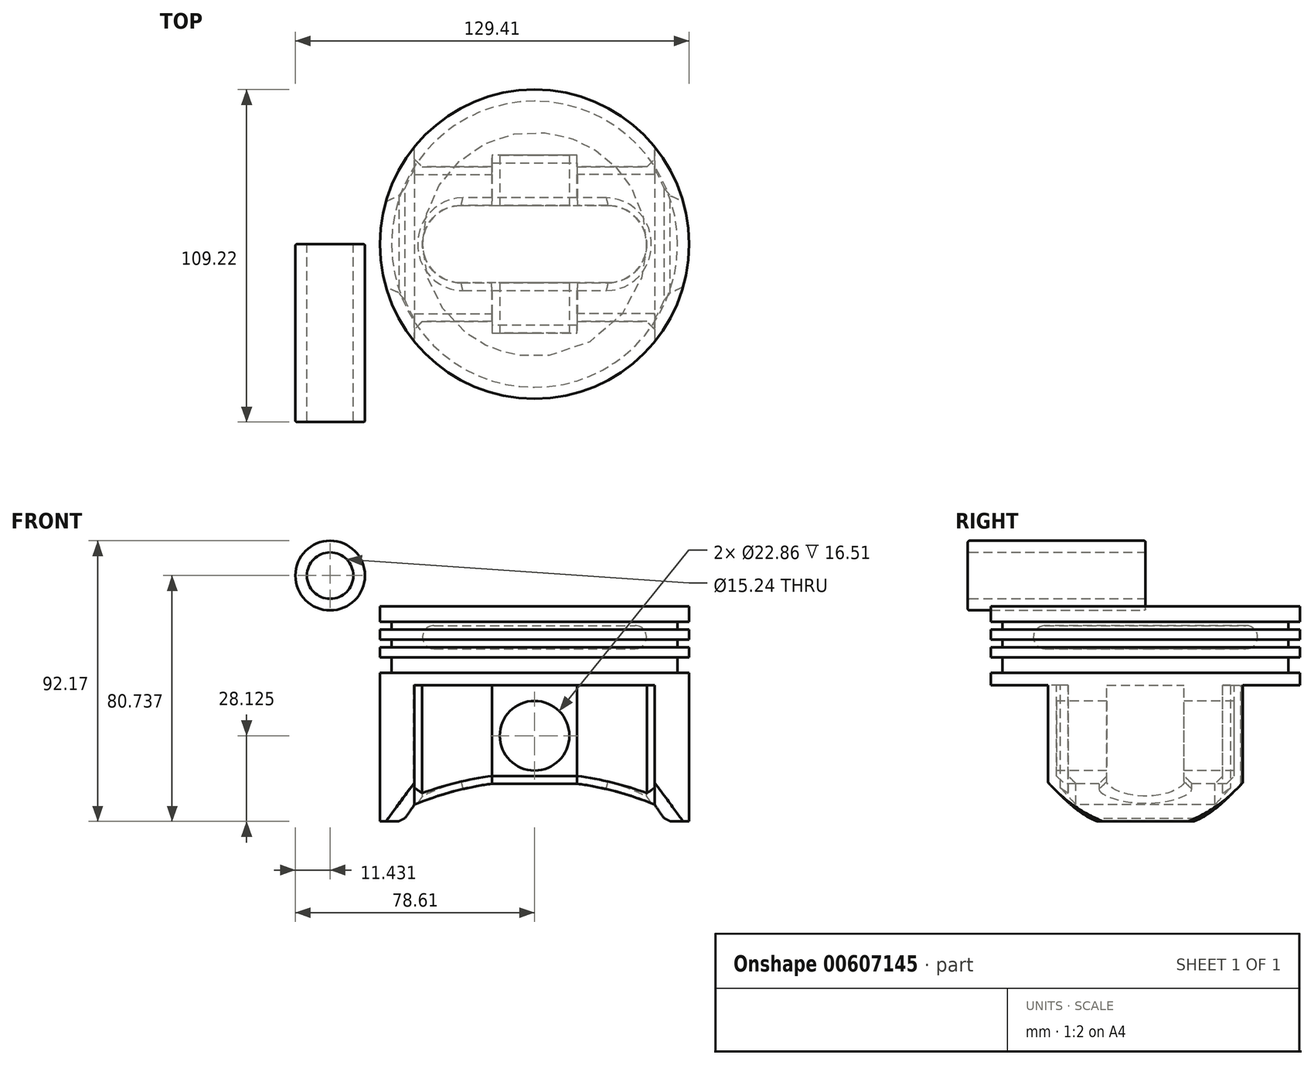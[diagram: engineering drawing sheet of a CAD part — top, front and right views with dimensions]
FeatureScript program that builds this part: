
annotation { "Feature Type Name" : "Feature", "Feature Type Description" : "" }
export const myFeature = defineFeature(function(context is Context, id is Id, definition is map)
    precondition{}
    {
        {
            var Q0;
            Q0=qCreatedBy(makeId("Front.planeOp"),FACE);
            var sketch = newSketch(context, id + "F0", { "sketchPlane" : qUnion([Q0])});
            skLineSegment(sketch, "E0", {"start": v(0, 42.54) * mm, "end": v(-50.8, 42.54) * mm});
            skLineSegment(sketch, "E1", {"start": v(-50.8, 42.54) * mm, "end": v(-50.8, 37.46) * mm});
            skLineSegment(sketch, "E2", {"start": v(-50.8, 37.46) * mm, "end": v(-47, 37.46) * mm});
            skLineSegment(sketch, "E3", {"start": v(-47, 37.46) * mm, "end": v(-47, 34.92) * mm});
            skLineSegment(sketch, "E4", {"start": v(-47, 34.92) * mm, "end": v(-50.8, 34.92) * mm});
            skLineSegment(sketch, "E5", {"start": v(-50.8, 34.92) * mm, "end": v(-50.8, 31.62) * mm});
            skLineSegment(sketch, "E6", {"start": v(-50.8, 31.62) * mm, "end": v(-47, 31.62) * mm});
            skLineSegment(sketch, "E7", {"start": v(-47, 31.62) * mm, "end": v(-47, 29.08) * mm});
            skLineSegment(sketch, "E8", {"start": v(-47, 29.08) * mm, "end": v(-50.8, 29.08) * mm});
            skLineSegment(sketch, "E9", {"start": v(-50.8, 29.08) * mm, "end": v(-50.8, 25.78) * mm});
            skLineSegment(sketch, "E10", {"start": v(-50.8, 25.78) * mm, "end": v(-47, 25.78) * mm});
            skLineSegment(sketch, "E11", {"start": v(-47, 25.78) * mm, "end": v(-47, 20.7) * mm});
            skLineSegment(sketch, "E12", {"start": v(-47, 20.7) * mm, "end": v(-50.8, 20.7) * mm});
            skLineSegment(sketch, "E13", {"start": v(-50.8, 20.7) * mm, "end": v(-50.8, 16.53) * mm});
            skLineSegment(sketch, "E14", {"start": v(-47, 24.5) * mm, "end": v(-50.23, 24.5) * mm, "construction": true});
            skLineSegment(sketch, "E15", {"start": v(-47, 21.97) * mm, "end": v(-49.28, 21.97) * mm, "construction": true});
            skLineSegment(sketch, "E16", {"start": v(-50.8, 16.53) * mm, "end": v(0, 16.53) * mm});
            skLineSegment(sketch, "E17", {"start": v(0, 16.53) * mm, "end": v(0, 42.54) * mm});
            skLineSegment(sketch, "E18", {"start": v(0, 36.19) * mm, "end": v(-33.02, 36.19) * mm});
            skLineSegment(sketch, "E19", {"start": v(-33.02, 28.57) * mm, "end": v(0, 28.57) * mm});
            skArc(sketch, "E20", {"start": v(-33.02, 36.19) * mm, "mid": v(-36.83, 32.38) * mm, "end": v(-33.02, 28.57) * mm});
            skSolve(sketch);
        }
        {
            var Q0;
            {var subQ0=sQuery(id+"F0.wireOp",EDGE,"E0");Q0=makeQuery(id+"F0.imprint","IMPRINT",FACE,{"disambiguationData":[TD([[makeQuery(id+"F0.imprint","IMPRINT",EDGE,{"derivedFrom":subQ0}),1.0]])]});}
            var Q1;
            Q1=sQuery(id+"F0.wireOp",EDGE,"E17");
            revolve(context, id + "F1", {"entities" : qUnion([Q0]), "axis" : qUnion([Q1]), "revolveType" : RevolveType.FULL});
        }
        {
            var Q0;
            Q0=makeQuery(id+"F1.opRevolve","SWEPT_FACE",FACE,{"disambiguationData":[OSD([sQuery(id+"F0.wireOp",EDGE,"E16")])]});
            var sketch = newSketch(context, id + "F2", { "sketchPlane" : qUnion([Q0])});
            skLineSegment(sketch, "E21", {"start": v(0, 12.7) * mm, "end": v(-24.13, 12.7) * mm});
            skLineSegment(sketch, "E22", {"start": v(-13.97, 25.4) * mm, "end": v(-39.45, 25.4) * mm});
            skLineSegment(sketch, "E23", {"start": v(-39.45, 25.4) * mm, "end": v(-39.45, 32) * mm});
            skLineSegment(sketch, "E24.MirrorCS", {"start": v(0, -12.7) * mm, "end": v(-24.13, -12.7) * mm});
            skLineSegment(sketch, "E25.MirrorCS", {"start": v(-13.97, -25.4) * mm, "end": v(-39.45, -25.4) * mm});
            skLineSegment(sketch, "E26.MirrorCS", {"start": v(-39.45, -25.4) * mm, "end": v(-39.45, -32) * mm});
            skArc(sketch, "E27", {"start": v(-24.13, 12.7) * mm, "mid": v(-36.83, 0) * mm, "end": v(-24.13, -12.7) * mm});
            skLineSegment(sketch, "E28.MirrorCS", {"start": v(13.97, 25.4) * mm, "end": v(39.45, 25.4) * mm});
            skLineSegment(sketch, "E29.MirrorCS", {"start": v(0, 12.7) * mm, "end": v(24.13, 12.7) * mm});
            skArc(sketch, "E30.MirrorCS", {"start": v(24.13, 12.7) * mm, "mid": v(36.83, 0) * mm, "end": v(24.13, -12.7) * mm});
            skLineSegment(sketch, "E31.MirrorCS", {"start": v(39.45, -25.4) * mm, "end": v(39.45, -32) * mm});
            skLineSegment(sketch, "E32.MirrorCS", {"start": v(13.97, -25.4) * mm, "end": v(39.45, -25.4) * mm});
            skLineSegment(sketch, "E33.MirrorCS", {"start": v(0, -12.7) * mm, "end": v(24.13, -12.7) * mm});
            skLineSegment(sketch, "E34.MirrorCS", {"start": v(39.45, 25.4) * mm, "end": v(39.45, 32) * mm});
            skLineSegment(sketch, "E35", {"start": v(-13.97, 25.4) * mm, "end": v(-13.97, 29.21) * mm});
            skLineSegment(sketch, "E36", {"start": v(-13.97, 29.21) * mm, "end": v(0, 29.21) * mm});
            skLineSegment(sketch, "E37.MirrorCS", {"start": v(13.97, 29.21) * mm, "end": v(0, 29.21) * mm});
            skLineSegment(sketch, "E38.MirrorCS", {"start": v(13.97, 25.4) * mm, "end": v(13.97, 29.21) * mm});
            skLineSegment(sketch, "E39.MirrorCS", {"start": v(-13.97, -29.21) * mm, "end": v(0, -29.21) * mm});
            skLineSegment(sketch, "E40.MirrorCS", {"start": v(-13.97, -25.4) * mm, "end": v(-13.97, -29.21) * mm});
            skLineSegment(sketch, "E41.MirrorCS", {"start": v(13.97, -29.21) * mm, "end": v(0, -29.21) * mm});
            skLineSegment(sketch, "E42.MirrorCS", {"start": v(13.97, -25.4) * mm, "end": v(13.97, -29.21) * mm});
            skPoint(sketch, "E43.orphan", {"position": v(0, 25.4) * mm});
            skPoint(sketch, "E44.orphan", {"position": v(0, -25.4) * mm});
            skSolve(sketch);
        }
        {
            var Q0;
            Q0=makeQuery(id+"F2.imprint","IMPRINT",FACE,{"disambiguationData":[TD([[makeQuery(id+"F2.imprint","IMPRINT",EDGE,{"derivedFrom":sQuery(id+"F2.wireOp",EDGE,"E21")}),-1.0]])]});
            extrude(context, id + "F3", {"entities" : qUnion([Q0]), "operationType" : NewBodyOperationType.ADD, "depth" : 50.8 * mm, "offsetDistance" : 25.4 * mm});
        }
        {
            var Q0;
            Q0=makeQuery(id+"F3.opExtrude","SWEPT_FACE",FACE,{"disambiguationData":[OSD([sQuery(id+"F2.wireOp",EDGE,"E36"),sQuery(id+"F2.wireOp",EDGE,"E37.MirrorCS")])]});
            var sketch = newSketch(context, id + "F4", { "sketchPlane" : qUnion([Q0])});
            skCircle(sketch, "E45", {"center": v(0, 0) * mm, "radius": 11.43 * mm});
            skLineSegment(sketch, "E46", {"start": v(-50.8, -34.27) * mm, "end": v(-50.8, 20.7) * mm});
            skLineSegment(sketch, "E47", {"start": v(50.8, 20.7) * mm, "end": v(50.8, -34.27) * mm});
            skPoint(sketch, "E48.0.end.orphan", {"position": v(-50.8, -34.27) * mm});
            skPoint(sketch, "E48.0.start.orphan", {"position": v(-39.45, -34.27) * mm});
            skPoint(sketch, "E49.0.end.orphan", {"position": v(50.8, -34.27) * mm});
            skPoint(sketch, "E49.0.start.orphan", {"position": v(39.45, -34.27) * mm});
            skPoint(sketch, "E50", {"position": v(-50.8, -28.13) * mm});
            skPoint(sketch, "E51", {"position": v(50.8, -28.13) * mm});
            skArc(sketch, "E52", {"start": v(39.45, -22.62) * mm, "mid": v(26.93, -18.38) * mm, "end": v(13.97, -15.76) * mm});
            skLineSegment(sketch, "E53", {"start": v(-13.97, -15.76) * mm, "end": v(13.97, -15.76) * mm});
            skArc(sketch, "E54.trimOffspring", {"start": v(-13.97, -15.76) * mm, "mid": v(-26.93, -18.38) * mm, "end": v(-39.45, -22.62) * mm});
            skLineSegment(sketch, "E55", {"start": v(-50.8, -28.13) * mm, "end": v(-43.3, -28.13) * mm});
            skLineSegment(sketch, "E56.MirrorCS", {"start": v(50.8, -28.13) * mm, "end": v(43.3, -28.13) * mm});
            skLineSegment(sketch, "E57", {"start": v(-50.8, -28.13) * mm, "end": v(-60.85, -30.62) * mm});
            skLineSegment(sketch, "E58", {"start": v(-60.85, -30.62) * mm, "end": v(-59.3, -53.17) * mm});
            skLineSegment(sketch, "E59", {"start": v(-59.3, -53.17) * mm, "end": v(61.9, -50.2) * mm});
            skLineSegment(sketch, "E60", {"start": v(61.9, -50.2) * mm, "end": v(64.49, -26.6) * mm});
            skLineSegment(sketch, "E61", {"start": v(64.49, -26.6) * mm, "end": v(50.8, -28.13) * mm});
            skLineSegment(sketch, "E62", {"start": v(43.3, -28.13) * mm, "end": v(39.45, -22.62) * mm});
            skPoint(sketch, "E63.MirrorCS.start.orphan", {"position": v(39.45, -28.13) * mm});
            skLineSegment(sketch, "E64.MirrorCS", {"start": v(-43.3, -28.13) * mm, "end": v(-39.45, -22.62) * mm});
            skPoint(sketch, "E65.start.orphan", {"position": v(-39.45, -28.13) * mm});
            skSolve(sketch);
        }
        {
            var Q0;
            {var subQ0=sQuery(id+"F4.wireOp",EDGE,"E52");Q0=makeQuery(id+"F4.imprint","IMPRINT",FACE,{"disambiguationData":[TD([[makeQuery(id+"F4.imprint","IMPRINT",EDGE,{"derivedFrom":subQ0}),1.0]])]});}
            var Q1;
            Q1=makeQuery(id+"F4.imprint","IMPRINT",FACE,{"disambiguationData":[TD([[makeQuery(id+"F4.imprint","IMPRINT",EDGE,{"derivedFrom":sQuery(id+"F4.wireOp",EDGE,"E45")}),1.0]])]});
            var Q2;
            {var subQ0=sQuery(id+"F4.wireOp",EDGE,"E53");Q2=makeQuery(id+"F4.imprint","IMPRINT",FACE,{"disambiguationData":[TD([[makeQuery(id+"F4.imprint","IMPRINT",EDGE,{"derivedFrom":subQ0}),-1.0]])]});}
            extrude(context, id + "F5", {"entities" : qUnion([Q0, Q1, Q2]), "operationType" : NewBodyOperationType.REMOVE, "oppositeDirection" : true, "depth" : 160.53 * mm, "offsetDistance" : 25.4 * mm, "symmetric" : true});
        }
        {
            var Q0;
            Q0=makeQuery(id+"F5.boolean.opBoolean","INTERSECT",EDGE,{"derivedFrom":[makeQuery(id+"F3.opExtrude","SWEPT_FACE",FACE,{"disambiguationData":[OSD([sQuery(id+"F2.wireOp",EDGE,"E30.MirrorCS")])]}),makeQuery(id+"F5.opExtrude","SWEPT_FACE",FACE,{"disambiguationData":[OSD([sQuery(id+"F4.wireOp",EDGE,"E52")])]})]});
            var Q1;
            Q1=makeQuery(id+"F5.boolean.opBoolean","INTERSECT",EDGE,{"derivedFrom":[makeQuery(id+"F3.opExtrude","SWEPT_FACE",FACE,{"disambiguationData":[OSD([sQuery(id+"F2.wireOp",EDGE,"E24.MirrorCS"),sQuery(id+"F2.wireOp",EDGE,"E33.MirrorCS")])]}),makeQuery(id+"F5.opExtrude","SWEPT_FACE",FACE,{"disambiguationData":[OSD([sQuery(id+"F4.wireOp",EDGE,"E53")])]})]});
            var Q2;
            Q2=makeQuery(id+"F5.boolean.opBoolean","INTERSECT",EDGE,{"derivedFrom":[makeQuery(id+"F3.opExtrude","SWEPT_FACE",FACE,{"disambiguationData":[OSD([sQuery(id+"F2.wireOp",EDGE,"E24.MirrorCS"),sQuery(id+"F2.wireOp",EDGE,"E33.MirrorCS")])]}),makeQuery(id+"F5.opExtrude","SWEPT_FACE",FACE,{"disambiguationData":[OSD([sQuery(id+"F4.wireOp",EDGE,"E54.trimOffspring")])]})]});
            var Q3;
            Q3=makeQuery(id+"F5.boolean.opBoolean","INTERSECT",EDGE,{"derivedFrom":[makeQuery(id+"F3.opExtrude","SWEPT_FACE",FACE,{"disambiguationData":[OSD([sQuery(id+"F2.wireOp",EDGE,"E21"),sQuery(id+"F2.wireOp",EDGE,"E29.MirrorCS")])]}),makeQuery(id+"F5.opExtrude","SWEPT_FACE",FACE,{"disambiguationData":[OSD([sQuery(id+"F4.wireOp",EDGE,"E53")])]})]});
            var Q4;
            Q4=makeQuery(id+"F5.boolean.opBoolean","INTERSECT",EDGE,{"derivedFrom":[makeQuery(id+"F3.opExtrude","SWEPT_FACE",FACE,{"disambiguationData":[OSD([sQuery(id+"F2.wireOp",EDGE,"E32.MirrorCS")])]}),makeQuery(id+"F5.opExtrude","SWEPT_FACE",FACE,{"disambiguationData":[OSD([sQuery(id+"F4.wireOp",EDGE,"E52")])]})]});
            var Q5;
            Q5=makeQuery(id+"F5.boolean.opBoolean","INTERSECT",EDGE,{"derivedFrom":[makeQuery(id+"F3.opExtrude","SWEPT_FACE",FACE,{"disambiguationData":[OSD([sQuery(id+"F2.wireOp",EDGE,"E25.MirrorCS")])]}),makeQuery(id+"F5.opExtrude","SWEPT_FACE",FACE,{"disambiguationData":[OSD([sQuery(id+"F4.wireOp",EDGE,"E54.trimOffspring")])]})]});
            var Q6;
            Q6=makeQuery(id+"F3.opExtrude","CAP_EDGE",EDGE,{"disambiguationData":[OSD([sQuery(id+"F2.wireOp",EDGE,"E25.MirrorCS")])],"isStart":true});
            var Q7;
            Q7=makeQuery(id+"F3.opExtrude","CAP_EDGE",EDGE,{"disambiguationData":[OSD([sQuery(id+"F2.wireOp",EDGE,"E32.MirrorCS")])],"isStart":true});
            var Q8;
            Q8=makeQuery(id+"F5.boolean.opBoolean","INTERSECT",EDGE,{"derivedFrom":[makeQuery(id+"F3.opExtrude","SWEPT_FACE",FACE,{"disambiguationData":[OSD([sQuery(id+"F2.wireOp",EDGE,"E22")])]}),makeQuery(id+"F5.opExtrude","SWEPT_FACE",FACE,{"disambiguationData":[OSD([sQuery(id+"F4.wireOp",EDGE,"E54.trimOffspring")])]})]});
            var Q9;
            Q9=makeQuery(id+"F5.boolean.opBoolean","INTERSECT",EDGE,{"derivedFrom":[makeQuery(id+"F3.opExtrude","SWEPT_FACE",FACE,{"disambiguationData":[OSD([sQuery(id+"F2.wireOp",EDGE,"E28.MirrorCS")])]}),makeQuery(id+"F5.opExtrude","SWEPT_FACE",FACE,{"disambiguationData":[OSD([sQuery(id+"F4.wireOp",EDGE,"E52")])]})]});
            var Q10;
            Q10=makeQuery(id+"F3.opExtrude","CAP_EDGE",EDGE,{"disambiguationData":[OSD([sQuery(id+"F2.wireOp",EDGE,"E28.MirrorCS")])],"isStart":true});
            var Q11;
            Q11=makeQuery(id+"F3.opExtrude","CAP_EDGE",EDGE,{"disambiguationData":[OSD([sQuery(id+"F2.wireOp",EDGE,"E22")])],"isStart":true});
            var Q12;
            Q12=makeQuery(id+"F3.opExtrude","CAP_EDGE",EDGE,{"disambiguationData":[OSD([sQuery(id+"F2.wireOp",EDGE,"E36"),sQuery(id+"F2.wireOp",EDGE,"E37.MirrorCS")])],"isStart":true});
            var Q13;
            Q13=makeQuery(id+"F3.opExtrude","CAP_EDGE",EDGE,{"disambiguationData":[OSD([sQuery(id+"F2.wireOp",EDGE,"E35")])],"isStart":true});
            var Q14;
            Q14=makeQuery(id+"F3.opExtrude","CAP_EDGE",EDGE,{"disambiguationData":[OSD([sQuery(id+"F2.wireOp",EDGE,"E38.MirrorCS")])],"isStart":true});
            var Q15;
            Q15=makeQuery(id+"F3.opExtrude","CAP_EDGE",EDGE,{"disambiguationData":[OSD([sQuery(id+"F2.wireOp",EDGE,"E39.MirrorCS"),sQuery(id+"F2.wireOp",EDGE,"E41.MirrorCS")])],"isStart":true});
            var Q16;
            Q16=makeQuery(id+"F3.opExtrude","CAP_EDGE",EDGE,{"disambiguationData":[OSD([sQuery(id+"F2.wireOp",EDGE,"E40.MirrorCS")])],"isStart":true});
            var Q17;
            Q17=makeQuery(id+"F3.opExtrude","CAP_EDGE",EDGE,{"disambiguationData":[OSD([sQuery(id+"F2.wireOp",EDGE,"E42.MirrorCS")])],"isStart":true});
            chamfer(context, id + "F6", {"entities" : qUnion([Q0, Q1, Q2, Q3, Q4, Q5, Q6, Q7, Q8, Q9, Q10, Q11, Q12, Q13, Q14, Q15, Q16, Q17]), "width" : 2.54 * mm, "tangentPropagation" : true});
        }
        {
            var Q0;
            Q0=makeQuery(id+"F3.opExtrude","SWEPT_EDGE",EDGE,{"disambiguationData":[OSD([sQuery(id+"F2.wireOp",EDGE,"E25.MirrorCS"),sQuery(id+"F2.wireOp",EDGE,"E26.MirrorCS")])]});
            var Q1;
            Q1=makeQuery(id+"F3.opExtrude","SWEPT_EDGE",EDGE,{"disambiguationData":[OSD([sQuery(id+"F2.wireOp",EDGE,"E31.MirrorCS"),sQuery(id+"F2.wireOp",EDGE,"E32.MirrorCS")])]});
            var Q2;
            Q2=makeQuery(id+"F5.boolean.opBoolean","INTERSECT",EDGE,{"derivedFrom":[makeQuery(id+"F3.opExtrude","SWEPT_FACE",FACE,{"disambiguationData":[OSD([sQuery(id+"F2.wireOp",EDGE,"E39.MirrorCS"),sQuery(id+"F2.wireOp",EDGE,"E41.MirrorCS")])]}),makeQuery(id+"F5.opExtrude","SWEPT_FACE",FACE,{"disambiguationData":[OSD([sQuery(id+"F4.wireOp",EDGE,"E53")])]})]});
            var Q3;
            {var subQ0=sQuery(id+"F4.wireOp",EDGE,"E53");Q3=makeQuery(id+"F5.boolean.opBoolean","COPY",EDGE,{"disambiguationData":[topologyDisambiguationEdgeConnected([makeQuery(id+"F3.opExtrude","SWEPT_FACE",FACE,{"disambiguationData":[OSD([sQuery(id+"F2.wireOp",EDGE,"E40.MirrorCS")])]}),makeQuery(id+"F5.opExtrude","SWEPT_FACE",FACE,{"disambiguationData":[OSD([subQ0])]})])],"derivedFrom":makeQuery(id+"F5.opExtrude","SWEPT_EDGE",EDGE,{"disambiguationData":[OSD([sQuery(id+"F2.wireOp",EDGE,"E35"),sQuery(id+"F2.wireOp",EDGE,"E36"),subQ0,sQuery(id+"F4.wireOp",EDGE,"E54.trimOffspring")])]})});}
            var Q4;
            {var subQ0=sQuery(id+"F4.wireOp",EDGE,"E53");Q4=makeQuery(id+"F5.boolean.opBoolean","COPY",EDGE,{"disambiguationData":[topologyDisambiguationEdgeConnected([makeQuery(id+"F3.opExtrude","SWEPT_FACE",FACE,{"disambiguationData":[OSD([sQuery(id+"F2.wireOp",EDGE,"E42.MirrorCS")])]}),makeQuery(id+"F5.opExtrude","SWEPT_FACE",FACE,{"disambiguationData":[OSD([subQ0])]})])],"derivedFrom":makeQuery(id+"F5.opExtrude","SWEPT_EDGE",EDGE,{"disambiguationData":[OSD([sQuery(id+"F2.wireOp",EDGE,"E37.MirrorCS"),sQuery(id+"F2.wireOp",EDGE,"E38.MirrorCS"),sQuery(id+"F4.wireOp",EDGE,"E52"),subQ0])]})});}
            var Q5;
            Q5=makeQuery(id+"F3.opExtrude","SWEPT_EDGE",EDGE,{"disambiguationData":[OSD([sQuery(id+"F2.wireOp",EDGE,"E28.MirrorCS"),sQuery(id+"F2.wireOp",EDGE,"E34.MirrorCS")])]});
            var Q6;
            Q6=makeQuery(id+"F3.opExtrude","SWEPT_EDGE",EDGE,{"disambiguationData":[OSD([sQuery(id+"F2.wireOp",EDGE,"E22"),sQuery(id+"F2.wireOp",EDGE,"E23")])]});
            var Q7;
            Q7=makeQuery(id+"F5.boolean.opBoolean","INTERSECT",EDGE,{"derivedFrom":[makeQuery(id+"F3.opExtrude","SWEPT_FACE",FACE,{"disambiguationData":[OSD([sQuery(id+"F2.wireOp",EDGE,"E36"),sQuery(id+"F2.wireOp",EDGE,"E37.MirrorCS")])]}),makeQuery(id+"F5.opExtrude","SWEPT_FACE",FACE,{"disambiguationData":[OSD([sQuery(id+"F4.wireOp",EDGE,"E53")])]})]});
            var Q8;
            {var subQ0=sQuery(id+"F2.wireOp",EDGE,"E38.MirrorCS");var subQ1=sQuery(id+"F4.wireOp",EDGE,"E53");Q8=makeQuery(id+"F5.boolean.opBoolean","COPY",EDGE,{"disambiguationData":[topologyDisambiguationEdgeConnected([makeQuery(id+"F3.opExtrude","SWEPT_FACE",FACE,{"disambiguationData":[OSD([subQ0])]}),makeQuery(id+"F5.opExtrude","SWEPT_FACE",FACE,{"disambiguationData":[OSD([subQ1])]})])],"derivedFrom":makeQuery(id+"F5.opExtrude","SWEPT_EDGE",EDGE,{"disambiguationData":[OSD([sQuery(id+"F2.wireOp",EDGE,"E37.MirrorCS"),subQ0,sQuery(id+"F4.wireOp",EDGE,"E52"),subQ1])]})});}
            var Q9;
            {var subQ0=sQuery(id+"F2.wireOp",EDGE,"E35");var subQ1=sQuery(id+"F4.wireOp",EDGE,"E53");Q9=makeQuery(id+"F5.boolean.opBoolean","COPY",EDGE,{"disambiguationData":[topologyDisambiguationEdgeConnected([makeQuery(id+"F3.opExtrude","SWEPT_FACE",FACE,{"disambiguationData":[OSD([subQ0])]}),makeQuery(id+"F5.opExtrude","SWEPT_FACE",FACE,{"disambiguationData":[OSD([subQ1])]})])],"derivedFrom":makeQuery(id+"F5.opExtrude","SWEPT_EDGE",EDGE,{"disambiguationData":[OSD([subQ0,sQuery(id+"F2.wireOp",EDGE,"E36"),subQ1,sQuery(id+"F4.wireOp",EDGE,"E54.trimOffspring")])]})});}
            var Q10;
            {var subQ0=sQuery(id+"F0.wireOp",EDGE,"E16");var subQ1=sQuery(id+"F0.wireOp",EDGE,"E13");var subQ2=makeQuery(id+"F1.opRevolve","SWEPT_EDGE",EDGE,{"disambiguationData":[OSD([subQ1,subQ0])]});Q10=makeQuery(id+"F5.boolean.opBoolean","INTERSECT",EDGE,{"disambiguationData":[OD(0.0)],"derivedFrom":[makeQuery(id+"F3.boolean.opBoolean","MERGE",FACE,{"derivedFrom":[makeQuery(id+"F1.opRevolve","SWEPT_FACE",FACE,{"disambiguationData":[OSD([subQ1])]}),makeQuery(id+"F3.opExtrude","SWEPT_FACE",FACE,{"disambiguationData":[OSD([subQ1,subQ0]),TDD([makeQuery(id+"F2.imprint","IMPRINT",EDGE,{"disambiguationData":[TD([[makeQuery(id+"F2.imprint","INTERSECT",VERTEX,{"derivedFrom":[subQ2,sQuery(id+"F2.wireOp",EDGE,"E23")]}),-1.0]])],"derivedFrom":subQ2})])]}),makeQuery(id+"F3.opExtrude","SWEPT_FACE",FACE,{"disambiguationData":[OSD([subQ1,subQ0]),TDD([makeQuery(id+"F2.imprint","IMPRINT",EDGE,{"disambiguationData":[TD([[makeQuery(id+"F2.imprint","INTERSECT",VERTEX,{"derivedFrom":[subQ2,sQuery(id+"F2.wireOp",EDGE,"E31.MirrorCS")]}),-1.0]])],"derivedFrom":subQ2})])]})]}),makeQuery(id+"F5.opExtrude","SWEPT_FACE",FACE,{"disambiguationData":[OSD([sQuery(id+"F4.wireOp",EDGE,"E62")])]})]});}
            var Q11;
            {var subQ0=sQuery(id+"F0.wireOp",EDGE,"E16");var subQ1=sQuery(id+"F0.wireOp",EDGE,"E13");var subQ2=makeQuery(id+"F1.opRevolve","SWEPT_EDGE",EDGE,{"disambiguationData":[OSD([subQ1,subQ0])]});Q11=makeQuery(id+"F5.boolean.opBoolean","INTERSECT",EDGE,{"disambiguationData":[OD(1.0)],"derivedFrom":[makeQuery(id+"F3.boolean.opBoolean","MERGE",FACE,{"derivedFrom":[makeQuery(id+"F1.opRevolve","SWEPT_FACE",FACE,{"disambiguationData":[OSD([subQ1])]}),makeQuery(id+"F3.opExtrude","SWEPT_FACE",FACE,{"disambiguationData":[OSD([subQ1,subQ0]),TDD([makeQuery(id+"F2.imprint","IMPRINT",EDGE,{"disambiguationData":[TD([[makeQuery(id+"F2.imprint","INTERSECT",VERTEX,{"derivedFrom":[subQ2,sQuery(id+"F2.wireOp",EDGE,"E23")]}),-1.0]])],"derivedFrom":subQ2})])]}),makeQuery(id+"F3.opExtrude","SWEPT_FACE",FACE,{"disambiguationData":[OSD([subQ1,subQ0]),TDD([makeQuery(id+"F2.imprint","IMPRINT",EDGE,{"disambiguationData":[TD([[makeQuery(id+"F2.imprint","INTERSECT",VERTEX,{"derivedFrom":[subQ2,sQuery(id+"F2.wireOp",EDGE,"E31.MirrorCS")]}),-1.0]])],"derivedFrom":subQ2})])]})]}),makeQuery(id+"F5.opExtrude","SWEPT_FACE",FACE,{"disambiguationData":[OSD([sQuery(id+"F4.wireOp",EDGE,"E64.MirrorCS")])]})]});}
            var Q12;
            {var subQ0=sQuery(id+"F0.wireOp",EDGE,"E16");var subQ1=sQuery(id+"F0.wireOp",EDGE,"E13");var subQ2=makeQuery(id+"F1.opRevolve","SWEPT_EDGE",EDGE,{"disambiguationData":[OSD([subQ1,subQ0])]});Q12=makeQuery(id+"F5.boolean.opBoolean","INTERSECT",EDGE,{"disambiguationData":[OD(1.0)],"derivedFrom":[makeQuery(id+"F3.boolean.opBoolean","MERGE",FACE,{"derivedFrom":[makeQuery(id+"F1.opRevolve","SWEPT_FACE",FACE,{"disambiguationData":[OSD([subQ1])]}),makeQuery(id+"F3.opExtrude","SWEPT_FACE",FACE,{"disambiguationData":[OSD([subQ1,subQ0]),TDD([makeQuery(id+"F2.imprint","IMPRINT",EDGE,{"disambiguationData":[TD([[makeQuery(id+"F2.imprint","INTERSECT",VERTEX,{"derivedFrom":[subQ2,sQuery(id+"F2.wireOp",EDGE,"E23")]}),-1.0]])],"derivedFrom":subQ2})])]}),makeQuery(id+"F3.opExtrude","SWEPT_FACE",FACE,{"disambiguationData":[OSD([subQ1,subQ0]),TDD([makeQuery(id+"F2.imprint","IMPRINT",EDGE,{"disambiguationData":[TD([[makeQuery(id+"F2.imprint","INTERSECT",VERTEX,{"derivedFrom":[subQ2,sQuery(id+"F2.wireOp",EDGE,"E31.MirrorCS")]}),-1.0]])],"derivedFrom":subQ2})])]})]}),makeQuery(id+"F5.opExtrude","SWEPT_FACE",FACE,{"disambiguationData":[OSD([sQuery(id+"F4.wireOp",EDGE,"E62")])]})]});}
            var Q13;
            {var subQ0=sQuery(id+"F0.wireOp",EDGE,"E16");var subQ1=sQuery(id+"F0.wireOp",EDGE,"E13");var subQ2=makeQuery(id+"F1.opRevolve","SWEPT_EDGE",EDGE,{"disambiguationData":[OSD([subQ1,subQ0])]});Q13=makeQuery(id+"F5.boolean.opBoolean","INTERSECT",EDGE,{"disambiguationData":[OD(0.0)],"derivedFrom":[makeQuery(id+"F3.boolean.opBoolean","MERGE",FACE,{"derivedFrom":[makeQuery(id+"F1.opRevolve","SWEPT_FACE",FACE,{"disambiguationData":[OSD([subQ1])]}),makeQuery(id+"F3.opExtrude","SWEPT_FACE",FACE,{"disambiguationData":[OSD([subQ1,subQ0]),TDD([makeQuery(id+"F2.imprint","IMPRINT",EDGE,{"disambiguationData":[TD([[makeQuery(id+"F2.imprint","INTERSECT",VERTEX,{"derivedFrom":[subQ2,sQuery(id+"F2.wireOp",EDGE,"E23")]}),-1.0]])],"derivedFrom":subQ2})])]}),makeQuery(id+"F3.opExtrude","SWEPT_FACE",FACE,{"disambiguationData":[OSD([subQ1,subQ0]),TDD([makeQuery(id+"F2.imprint","IMPRINT",EDGE,{"disambiguationData":[TD([[makeQuery(id+"F2.imprint","INTERSECT",VERTEX,{"derivedFrom":[subQ2,sQuery(id+"F2.wireOp",EDGE,"E31.MirrorCS")]}),-1.0]])],"derivedFrom":subQ2})])]})]}),makeQuery(id+"F5.opExtrude","SWEPT_FACE",FACE,{"disambiguationData":[OSD([sQuery(id+"F4.wireOp",EDGE,"E64.MirrorCS")])]})]});}
            var Q14;
            Q14=makeQuery(id+"F5.boolean.opBoolean","COPY",EDGE,{"derivedFrom":makeQuery(id+"F5.opExtrude","SWEPT_EDGE",EDGE,{"disambiguationData":[OSD([sQuery(id+"F4.wireOp",EDGE,"E55"),sQuery(id+"F4.wireOp",EDGE,"E64.MirrorCS")])]})});
            var Q15;
            Q15=makeQuery(id+"F5.boolean.opBoolean","COPY",EDGE,{"derivedFrom":makeQuery(id+"F5.opExtrude","SWEPT_EDGE",EDGE,{"disambiguationData":[OSD([sQuery(id+"F4.wireOp",EDGE,"E56.MirrorCS"),sQuery(id+"F4.wireOp",EDGE,"E62")])]})});
            chamfer(context, id + "F7", {"entities" : qUnion([Q0, Q1, Q2, Q3, Q4, Q5, Q6, Q7, Q8, Q9, Q10, Q11, Q12, Q13, Q14, Q15]), "width" : 2.54 * mm, "tangentPropagation" : true});
        }
        {
            var Q0;
            Q0=makeQuery(id+"F3.opExtrude","SWEPT_EDGE",EDGE,{"disambiguationData":[OSD([sQuery(id+"F0.wireOp",EDGE,"E13"),sQuery(id+"F0.wireOp",EDGE,"E16"),sQuery(id+"F2.wireOp",EDGE,"E26.MirrorCS")])]});
            chamfer(context, id + "F8", {"entities" : qUnion([Q0]), "width" : 0.25 * mm, "tangentPropagation" : true});
        }
        {
            var Q0;
            Q0=qCreatedBy(makeId("Front.planeOp"),FACE);
            var sketch = newSketch(context, id + "F9", { "sketchPlane" : qUnion([Q0])});
            skCircle(sketch, "E66", {"center": v(-67.18, 52.6) * mm, "radius": 11.43 * mm});
            skCircle(sketch, "E67.0", {"center": v(-67.18, 52.6) * mm, "radius": 7.62 * mm});
            skSolve(sketch);
        }
        {
            var Q0;
            Q0=makeQuery(id+"F9.imprint","IMPRINT",FACE,{"disambiguationData":[TD([[makeQuery(id+"F9.imprint","IMPRINT",EDGE,{"derivedFrom":sQuery(id+"F9.wireOp",EDGE,"E66")}),1.0]])]});
            extrude(context, id + "F10", {"entities" : qUnion([Q0]), "depth" : 58.42 * mm, "offsetDistance" : 25.4 * mm});
        }
        {
            var Q0;
            Q0=makeQuery(id+"F10.opExtrude","SWEPT_FACE",FACE,{"disambiguationData":[OSD([sQuery(id+"F9.wireOp",EDGE,"E66")])]});
            var Q1;
            Q1=makeQuery(id+"F10.opExtrude","CAP_FACE",FACE,{"disambiguationData":[OSD([sQuery(id+"F9.wireOp",EDGE,"E66"),sQuery(id+"F9.wireOp",EDGE,"E67.0")])],"isStart":false});
            var Q2;
            Q2=makeQuery(id+"F10.opExtrude","CAP_FACE",FACE,{"disambiguationData":[OSD([sQuery(id+"F9.wireOp",EDGE,"E66"),sQuery(id+"F9.wireOp",EDGE,"E67.0")])],"isStart":true});
            fillet(context, id + "F11", {"entities" : qUnion([Q0, Q1, Q2]), "radius" : 0.5 * mm, "tangentPropagation" : true, "allowEdgeOverflow" : false});
        }
    });
